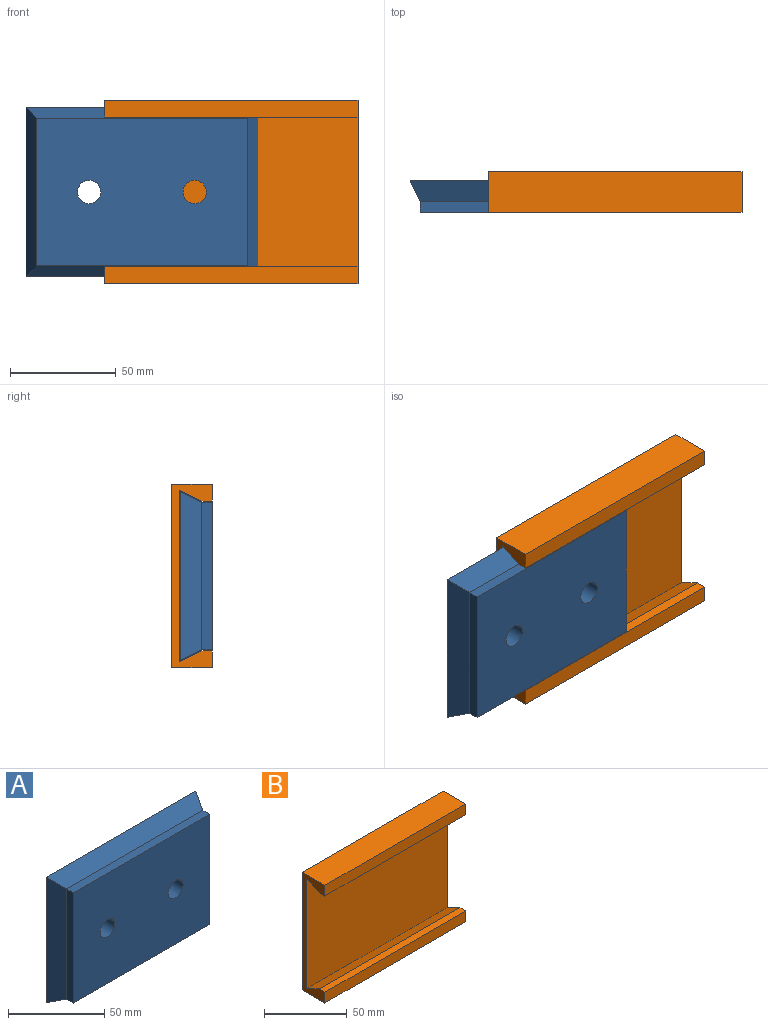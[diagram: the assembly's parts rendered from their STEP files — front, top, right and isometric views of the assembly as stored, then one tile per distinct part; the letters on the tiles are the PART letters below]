
ASSEMBLY  parts=2 mates=1
PART A: 12 faces, bbox 109.8x15x79.8 mm
  f0: plane 79.75x10mm, normal (-0.9,-0.44,0), area 833.1mm2, adj f1,f3,f4,f5
  f1: plane 109.75x10mm, normal (0,-0.44,-0.9), area 1166.9mm2, adj f0,f2,f4,f6
  f2: plane 79.75x10mm, normal (0.9,-0.44,0), area 833.1mm2, adj f1,f3,f4,f7
  f3: plane 109.75x10mm, normal (0,-0.44,0.9), area 1166.9mm2, adj f0,f2,f4,f8
  f4: plane 109.75x79.75mm, normal (0,1,0), area 8563.4mm2, adj f0,f1,f2,f3,f10,f11
  f5: plane 70x5mm, normal (-1,0,0), area 350mm2, adj f0,f6,f8,f9
  f6: plane 100x5mm, normal (0,0,-1), area 500mm2, adj f1,f5,f7,f9
  f7: plane 70x5mm, normal (1,0,0), area 350mm2, adj f2,f6,f8,f9
  f8: plane 100x5mm, normal (0,0,1), area 500mm2, adj f3,f5,f7,f9
  f9: plane 100x70mm, normal (0,-1,0), area 6809.9mm2, adj f5,f6,f7,f8,f10,f11
  f10: cylinder r=5.5mm len=15mm, axis (0,-1,0), area 518.4mm2, adj f4,f9
  f11: cylinder r=5.5mm len=15mm, axis (0,-1,0), area 518.4mm2, adj f4,f9
PART B: 12 faces, bbox 120x19.2x86.8 mm
  f0: plane 120x10.62mm, normal (0,0.44,-0.9), area 1417.3mm2, adj f1,f9,f10,f11
  f1: plane 120x81.36mm, normal (0,-1,0), area 9762.6mm2, adj f0,f2,f10,f11
  f2: plane 120x10.62mm, normal (0,0.44,0.9), area 1417.3mm2, adj f1,f3,f10,f11
  f3: plane 120x4.88mm, normal (0,0,1), area 586.1mm2, adj f2,f4,f10,f11
  f4: plane 120x7.92mm, normal (0,-1,0), area 950.2mm2, adj f3,f5,f10,f11
  f5: plane 120x19.23mm, normal (0,0,-1), area 2308.1mm2, adj f4,f6,f10,f11
  f6: plane 120x86.84mm, normal (0,1,0), area 10420.4mm2, adj f5,f7,f10,f11
  f7: plane 120x19.23mm, normal (0,0,1), area 2308.1mm2, adj f6,f8,f10,f11
  f8: plane 120x7.92mm, normal (0,-1,0), area 950.2mm2, adj f7,f9,f10,f11
  f9: plane 120x4.88mm, normal (0,0,-1), area 586.1mm2, adj f0,f8,f10,f11
  f10: plane 86.84x19.23mm, normal (1,0,0), area 514.8mm2, adj f0,f1,f2,f3,f4,f5,f6,f7
  f11: plane 86.84x19.23mm, normal (-1,0,0), area 514.8mm2, adj f0,f1,f2,f3,f4,f5,f6,f7
PLACE A t=(-4.4,39.02,15.97)mm
PLACE B t=(37.94,39.02,15.97)mm fixed
MATE slider A.f7 <-> B.f10  axis (1,0,0) through (45.6,36.52,15.97)mm
